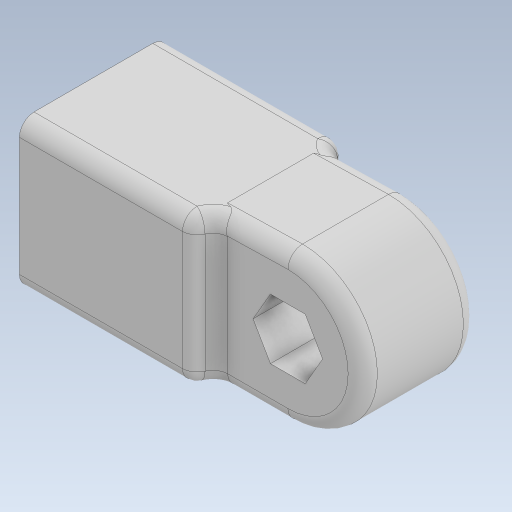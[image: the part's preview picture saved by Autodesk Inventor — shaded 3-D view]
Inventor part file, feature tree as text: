
AUTODESK INVENTOR PART (.ipt)
format: ipt  version: 2023 (Build 270158000, 158)  size: 222,208 bytes
history: native  units: in
note: dims shown in document units (in); Inventor stores cm internally (conversion verified against a paired STEP export)
features: extrude x2, fillet x2, sketch x2, shell x1, plane x1
ambient origin geometry x8: Origin, YZ Plane, XZ Plane, XY Plane, X Axis, Y Axis, Z Axis, Center Point
bodies: Solid1 (feature_tree)
feature tree (8):
  extrude  "Extrusion1"  Depth=1.0in
  shell  "Shell1"  Thickness=0.0075in
  plane  "Work Plane1"
  extrude  "Extrusion2"  Depth=0.125in TaperAngle=0.0deg
  fillet  "Fillet2"  Radius=0.125in
  fillet  "Fillet3"  [1 undecoded]
  sketch  "Sketch1"  dims[d0=1.0in d1=1.0in d2=0.0075in]
  sketch  "Sketch4"  dims[d3=0.125in d4=1.5in d5=0.0in d6=0.125in d7=-0.155in d8=0.515in d10=0.985in d11=0.0in d13=0.125in d14=0.125in]
note: 1 required parameter value undecoded (feature->parameter linkage not recoverable at this tier; creation-order binding heuristic only, values carry confidence <= 0.55)
